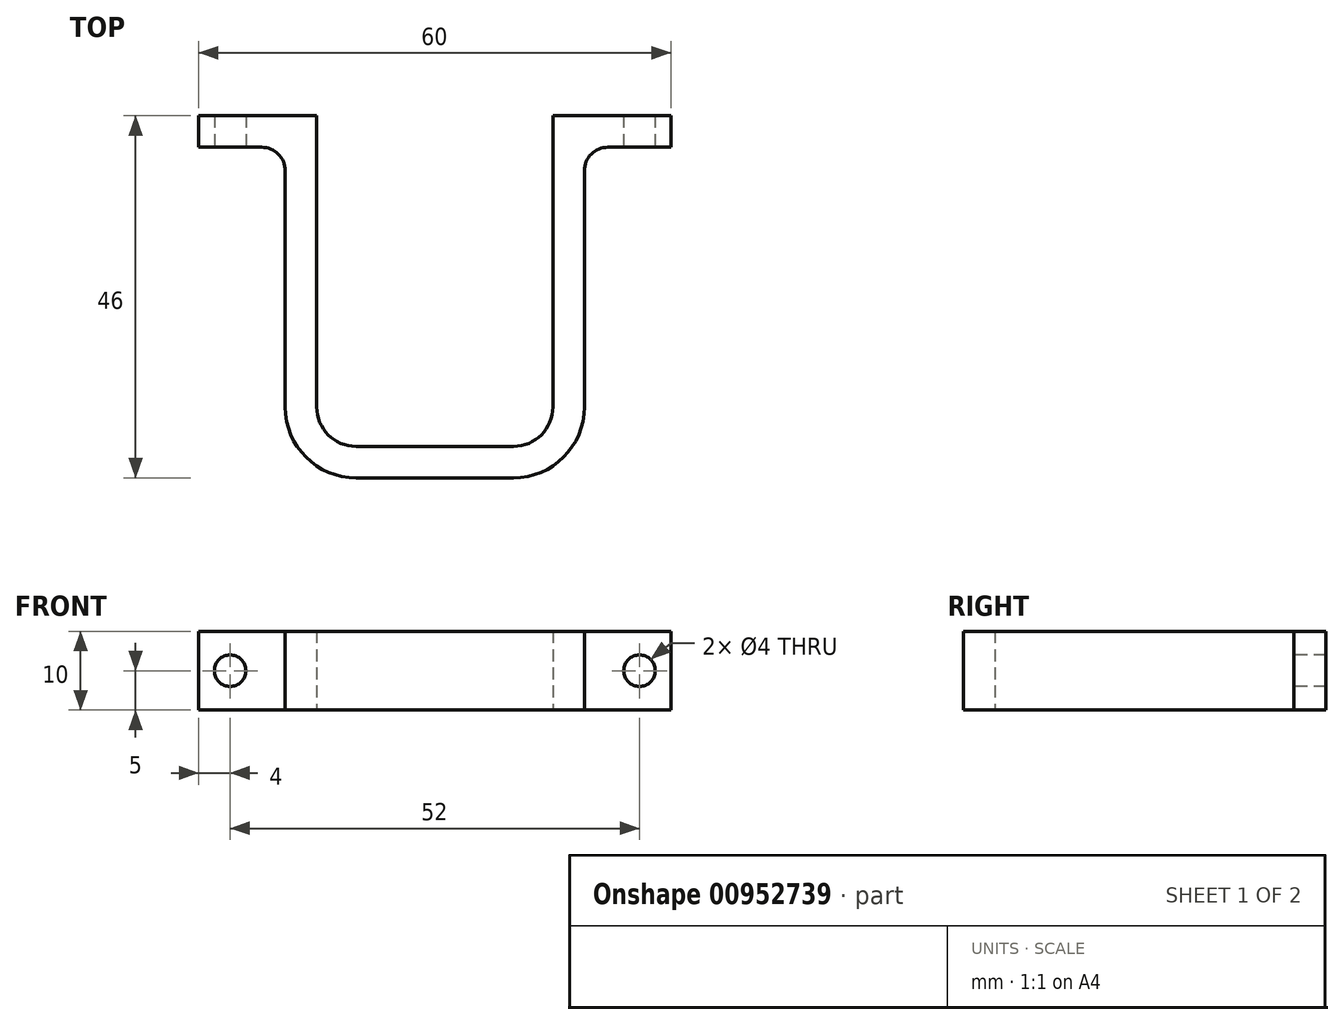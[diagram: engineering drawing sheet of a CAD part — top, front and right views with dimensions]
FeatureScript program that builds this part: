
annotation { "Feature Type Name" : "Feature", "Feature Type Description" : "" }
export const myFeature = defineFeature(function(context is Context, id is Id, definition is map)
    precondition{}
    {
        {
            var Q0;
            Q0=qCreatedBy(makeId("Top.planeOp"),FACE);
            var sketch = newSketch(context, id + "F0", { "sketchPlane" : qUnion([Q0])});
            skLineSegment(sketch, "E0", {"start": v(0, 0) * mm, "end": v(0, -37) * mm});
            skLineSegment(sketch, "E1", {"start": v(5, -42) * mm, "end": v(25, -42) * mm});
            skLineSegment(sketch, "E2", {"start": v(30, -37) * mm, "end": v(30, 0) * mm});
            skLineSegment(sketch, "E3", {"start": v(30, 0) * mm, "end": v(45, 0) * mm});
            skLineSegment(sketch, "E4", {"start": v(0, 0) * mm, "end": v(-15, 0) * mm});
            skPoint(sketch, "E5.visualSharp", {"position": v(0, -42) * mm});
            skArc(sketch, "E5.filletArc", {"start": v(0, -37) * mm, "mid": v(1.46, -40.54) * mm, "end": v(5, -42) * mm});
            skPoint(sketch, "E6.visualSharp", {"position": v(30, -42) * mm});
            skArc(sketch, "E6.filletArc", {"start": v(25, -42) * mm, "mid": v(28.54, -40.54) * mm, "end": v(30, -37) * mm});
            skLineSegment(sketch, "E7.0", {"start": v(-7, -4) * mm, "end": v(-15, -4) * mm});
            skLineSegment(sketch, "E7.1", {"start": v(-4, -7) * mm, "end": v(-4, -37) * mm});
            skArc(sketch, "E7.2", {"start": v(-4, -37) * mm, "mid": v(-1.36, -43.36) * mm, "end": v(5, -46) * mm});
            skLineSegment(sketch, "E7.3", {"start": v(37, -4) * mm, "end": v(45, -4) * mm});
            skLineSegment(sketch, "E7.4", {"start": v(34, -37) * mm, "end": v(34, -7) * mm});
            skArc(sketch, "E7.5", {"start": v(25, -46) * mm, "mid": v(31.36, -43.36) * mm, "end": v(34, -37) * mm});
            skLineSegment(sketch, "E7.6", {"start": v(5, -46) * mm, "end": v(25, -46) * mm});
            skPoint(sketch, "E8.visualSharp", {"position": v(34, -4) * mm});
            skArc(sketch, "E8.filletArc", {"start": v(37, -4) * mm, "mid": v(34.88, -4.88) * mm, "end": v(34, -7) * mm});
            skPoint(sketch, "E9.visualSharp", {"position": v(-4, -4) * mm});
            skArc(sketch, "E9.filletArc", {"start": v(-4, -7) * mm, "mid": v(-4.88, -4.88) * mm, "end": v(-7, -4) * mm});
            skLineSegment(sketch, "E10", {"start": v(45, -4) * mm, "end": v(45, 0) * mm});
            skLineSegment(sketch, "E11", {"start": v(-15, 0) * mm, "end": v(-15, -4) * mm});
            skSolve(sketch);
        }
        {
            var Q0;
            Q0=makeQuery(id+"F0.imprint","IMPRINT",FACE,{"disambiguationData":[TD([[makeQuery(id+"F0.imprint","IMPRINT",EDGE,{"derivedFrom":sQuery(id+"F0.wireOp",EDGE,"E0")}),-1.0]])]});
            extrude(context, id + "F1", {"entities" : qUnion([Q0]), "depth" : 10 * mm, "offsetDistance" : 25 * mm});
        }
        {
            var Q0;
            Q0=makeQuery(id+"F1.opExtrude","SWEPT_FACE",FACE,{"disambiguationData":[OSD([sQuery(id+"F0.wireOp",EDGE,"E7.0")])]});
            var sketch = newSketch(context, id + "F2", { "sketchPlane" : qUnion([Q0])});
            skCircle(sketch, "E12", {"center": v(-11, 5) * mm, "radius": 2 * mm});
            skPoint(sketch, "E12.centerSnap0", {"position": v(-15, 5) * mm});
            skCircle(sketch, "E13", {"center": v(41, 5) * mm, "radius": 2 * mm});
            skSolve(sketch);
        }
        {
            var Q0;
            Q0=makeQuery(id+"F2.imprint","IMPRINT",FACE,{"disambiguationData":[TD([[makeQuery(id+"F2.imprint","IMPRINT",EDGE,{"derivedFrom":sQuery(id+"F2.wireOp",EDGE,"E12")}),1.0]])]});
            var Q1;
            Q1=makeQuery(id+"F2.imprint","IMPRINT",FACE,{"disambiguationData":[TD([[makeQuery(id+"F2.imprint","IMPRINT",EDGE,{"derivedFrom":sQuery(id+"F2.wireOp",EDGE,"E13")}),1.0]])]});
            extrude(context, id + "F3", {"entities" : qUnion([Q0, Q1]), "operationType" : NewBodyOperationType.REMOVE, "oppositeDirection" : true, "depth" : 4 * mm, "offsetDistance" : 25 * mm});
        }
    });
